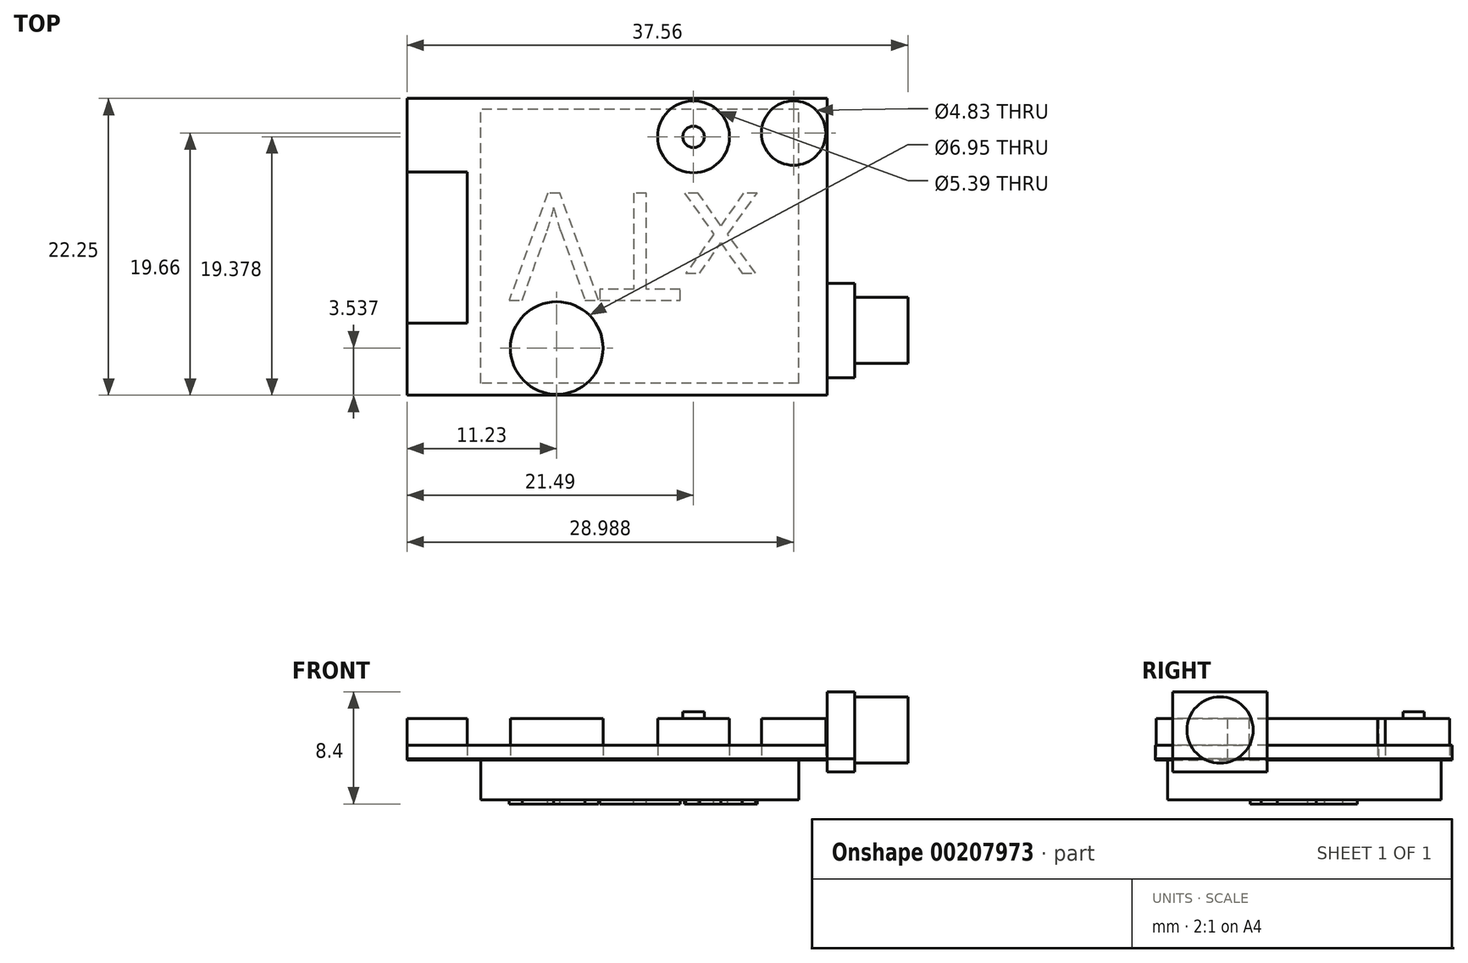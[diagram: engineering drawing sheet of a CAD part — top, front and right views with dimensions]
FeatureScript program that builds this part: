
annotation { "Feature Type Name" : "Feature", "Feature Type Description" : "" }
export const myFeature = defineFeature(function(context is Context, id is Id, definition is map)
    precondition{}
    {
        {
            var Q0;
            Q0=qCreatedBy(makeId("Top.planeOp"),FACE);
            var sketch = newSketch(context, id + "F0", { "sketchPlane" : qUnion([Q0])});
            skLineSegment(sketch, "E0.bottom", {"start": v(38.2, 11.57) * mm, "end": v(6.7, 11.57) * mm});
            skLineSegment(sketch, "E0.top", {"start": v(38.2, 33.82) * mm, "end": v(6.7, 33.82) * mm});
            skLineSegment(sketch, "E0.left", {"start": v(38.2, 11.57) * mm, "end": v(38.2, 33.82) * mm});
            skLineSegment(sketch, "E0.right", {"start": v(6.7, 11.57) * mm, "end": v(6.7, 33.82) * mm});
            skLineSegment(sketch, "E1.bottom", {"start": v(6.7, 28.3) * mm, "end": v(11.22, 28.3) * mm});
            skLineSegment(sketch, "E1.top", {"start": v(6.7, 16.97) * mm, "end": v(11.22, 16.97) * mm});
            skLineSegment(sketch, "E1.left", {"start": v(6.7, 28.3) * mm, "end": v(6.7, 16.97) * mm});
            skLineSegment(sketch, "E1.right", {"start": v(11.22, 28.3) * mm, "end": v(11.22, 16.97) * mm});
            skCircle(sketch, "E2", {"center": v(28.19, 30.95) * mm, "radius": 2.7 * mm});
            skCircle(sketch, "E3", {"center": v(35.69, 31.23) * mm, "radius": 2.41 * mm});
            skCircle(sketch, "E4", {"center": v(17.93, 15.1) * mm, "radius": 3.47 * mm});
            skLineSegment(sketch, "E5", {"start": v(38.2, 19.97) * mm, "end": v(40.26, 19.97) * mm});
            skLineSegment(sketch, "E6", {"start": v(40.26, 19.97) * mm, "end": v(40.26, 12.89) * mm});
            skLineSegment(sketch, "E7", {"start": v(40.26, 12.89) * mm, "end": v(38.2, 12.89) * mm});
            skSolve(sketch);
        }
        {
            var Q0;
            Q0=makeQuery(id+"F0.imprint","IMPRINT",FACE,{"disambiguationData":[TD([[makeQuery(id+"F0.imprint","IMPRINT",EDGE,{"derivedFrom":sQuery(id+"F0.wireOp",EDGE,"E1.bottom")}),-1.0]])]});
            var Q1;
            Q1=makeQuery(id+"F0.imprint","IMPRINT",FACE,{"disambiguationData":[TD([[makeQuery(id+"F0.imprint","IMPRINT",EDGE,{"derivedFrom":sQuery(id+"F0.wireOp",EDGE,"E4")}),1.0]])]});
            var Q2;
            Q2=makeQuery(id+"F0.imprint","IMPRINT",FACE,{"disambiguationData":[TD([[makeQuery(id+"F0.imprint","IMPRINT",EDGE,{"derivedFrom":sQuery(id+"F0.wireOp",EDGE,"E2")}),1.0]])]});
            var Q3;
            Q3=makeQuery(id+"F0.imprint","IMPRINT",FACE,{"disambiguationData":[TD([[makeQuery(id+"F0.imprint","IMPRINT",EDGE,{"derivedFrom":sQuery(id+"F0.wireOp",EDGE,"E3")}),1.0]])]});
            extrude(context, id + "F1", {"entities" : qUnion([Q0, Q1, Q2, Q3]), "depth" : 3 * mm});
        }
        {
            var Q0;
            Q0 = qSketchRegion(id + "F0", true);
            extrude(context, id + "F2", {"entities" : qUnion([Q0]), "depth" : 1 * mm});
        }
        {
            var Q0;
            Q0=makeQuery(id+"F2.opExtrude","CAP_FACE",FACE,{"disambiguationData":[OSD([sQuery(id+"F0.wireOp",EDGE,"E0.bottom"),sQuery(id+"F0.wireOp",EDGE,"E0.top"),sQuery(id+"F0.wireOp",EDGE,"E0.left"),sQuery(id+"F0.wireOp",EDGE,"E0.right"),sQuery(id+"F0.wireOp",EDGE,"E1.left"),sQuery(id+"F0.wireOp",EDGE,"E2"),sQuery(id+"F0.wireOp",EDGE,"E3"),sQuery(id+"F0.wireOp",EDGE,"E4")])],"isStart":true});
            var sketch = newSketch(context, id + "F3", { "sketchPlane" : qUnion([Q0])});
            skLineSegment(sketch, "E8.bottom", {"start": v(38.2, -33.82) * mm, "end": v(6.7, -33.82) * mm});
            skLineSegment(sketch, "E8.top", {"start": v(38.2, -11.57) * mm, "end": v(6.7, -11.57) * mm});
            skLineSegment(sketch, "E8.left", {"start": v(38.2, -33.82) * mm, "end": v(38.2, -11.57) * mm});
            skLineSegment(sketch, "E8.right", {"start": v(6.7, -33.82) * mm, "end": v(6.7, -11.57) * mm});
            skSolve(sketch);
        }
        {
            var Q0;
            Q0=makeQuery(id+"F1.opExtrude","CAP_FACE",FACE,{"disambiguationData":[OSD([sQuery(id+"F0.wireOp",EDGE,"E2")])],"isStart":false});
            var sketch = newSketch(context, id + "F4", { "sketchPlane" : qUnion([Q0])});
            skCircle(sketch, "E9", {"center": v(28.19, 30.95) * mm, "radius": 0.8 * mm});
            skSolve(sketch);
        }
        {
            var Q0;
            Q0=makeQuery(id+"F4.imprint","IMPRINT",FACE,{"disambiguationData":[TD([[makeQuery(id+"F4.imprint","IMPRINT",EDGE,{"derivedFrom":sQuery(id+"F4.wireOp",EDGE,"E9")}),1.0]])]});
            extrude(context, id + "F5", {"entities" : qUnion([Q0]), "operationType" : NewBodyOperationType.ADD, "depth" : .5 * mm});
        }
        {
            var Q0;
            Q0=makeQuery(id+"F3.imprint","IMPRINT",FACE,{"disambiguationData":[TD([[makeQuery(id+"F3.imprint","IMPRINT",EDGE,{"derivedFrom":sQuery(id+"F3.wireOp",EDGE,"E8.bottom")}),-1.0]])]});
            var Q1;
            Q1=makeQuery(id+"F3.imprint","IMPRINT",FACE,{"disambiguationData":[TD([[makeQuery(id+"F3.imprint","IMPRINT",EDGE,{"derivedFrom":makeQuery(id+"F2.opExtrude","CAP_EDGE",EDGE,{"disambiguationData":[OSD([sQuery(id+"F0.wireOp",EDGE,"E3")])],"isStart":true})}),-1.0]])]});
            var Q2;
            Q2=makeQuery(id+"F3.imprint","IMPRINT",FACE,{"disambiguationData":[TD([[makeQuery(id+"F3.imprint","IMPRINT",EDGE,{"derivedFrom":makeQuery(id+"F2.opExtrude","CAP_EDGE",EDGE,{"disambiguationData":[OSD([sQuery(id+"F0.wireOp",EDGE,"E2")])],"isStart":true})}),-1.0]])]});
            var Q3;
            Q3=makeQuery(id+"F3.imprint","IMPRINT",FACE,{"disambiguationData":[TD([[makeQuery(id+"F3.imprint","IMPRINT",EDGE,{"derivedFrom":makeQuery(id+"F2.opExtrude","CAP_EDGE",EDGE,{"disambiguationData":[OSD([sQuery(id+"F0.wireOp",EDGE,"E4")])],"isStart":true})}),-1.0]])]});
            extrude(context, id + "F6", {"entities" : qUnion([Q0, Q1, Q2, Q3]), "depth" : .1 * mm});
        }
        {
            var Q0;
            Q0=makeQuery(id+"F6.opExtrude","CAP_FACE",FACE,{"disambiguationData":[OSD([sQuery(id+"F3.wireOp",EDGE,"E8.bottom"),sQuery(id+"F3.wireOp",EDGE,"E8.top"),sQuery(id+"F3.wireOp",EDGE,"E8.left"),sQuery(id+"F3.wireOp",EDGE,"E8.right")])],"isStart":false});
            var sketch = newSketch(context, id + "F7", { "sketchPlane" : qUnion([Q0])});
            skLineSegment(sketch, "E10.bottom", {"start": v(36.07, -12.48) * mm, "end": v(12.23, -12.48) * mm});
            skLineSegment(sketch, "E10.top", {"start": v(36.07, -33) * mm, "end": v(12.23, -33) * mm});
            skLineSegment(sketch, "E10.left", {"start": v(36.07, -12.48) * mm, "end": v(36.07, -33) * mm});
            skLineSegment(sketch, "E10.right", {"start": v(12.23, -12.48) * mm, "end": v(12.23, -33) * mm});
            skSolve(sketch);
        }
        {
            var Q0;
            Q0=makeQuery(id+"F7.imprint","IMPRINT",FACE,{"disambiguationData":[TD([[makeQuery(id+"F7.imprint","IMPRINT",EDGE,{"derivedFrom":sQuery(id+"F7.wireOp",EDGE,"E10.bottom")}),1.0]])]});
            extrude(context, id + "F8", {"entities" : qUnion([Q0]), "operationType" : NewBodyOperationType.ADD, "depth" : 3 * mm});
        }
        {
            var Q0;
            Q0=makeQuery(id+"F8.opExtrude","CAP_FACE",FACE,{"disambiguationData":[OSD([sQuery(id+"F7.wireOp",EDGE,"E10.bottom"),sQuery(id+"F7.wireOp",EDGE,"E10.top"),sQuery(id+"F7.wireOp",EDGE,"E10.left"),sQuery(id+"F7.wireOp",EDGE,"E10.right")])],"isStart":false});
            var sketch = newSketch(context, id + "F9", { "sketchPlane" : qUnion([Q0])});
            skText(sketch, "E11", { "text": "VTx", "fontName": "OpenSans-Regular.ttf"});
            const initialGuessF9  = {"E11": [0.01437, -0.02673, 1, 0, 0.0081]};
            skSetInitialGuess(sketch, initialGuessF9);
            skSolve(sketch);
        }
        {
            var Q0;
            Q0=makeQuery(id+"F9.imprint","IMPRINT",FACE,{"disambiguationData":[TD([[makeQuery(id+"F9.imprint","IMPRINT",EDGE,{"derivedFrom":sQuery(id+"F9.wireOp",EDGE,"E11.sketch_text.stroke-0")}),-1.0]])]});
            var Q1;
            Q1=makeQuery(id+"F9.imprint","IMPRINT",FACE,{"disambiguationData":[TD([[makeQuery(id+"F9.imprint","IMPRINT",EDGE,{"derivedFrom":sQuery(id+"F9.wireOp",EDGE,"E11.sketch_text.stroke-9")}),-1.0]])]});
            var Q2;
            Q2=makeQuery(id+"F9.imprint","IMPRINT",FACE,{"disambiguationData":[TD([[makeQuery(id+"F9.imprint","IMPRINT",EDGE,{"derivedFrom":sQuery(id+"F9.wireOp",EDGE,"E11.sketch_text.stroke-17")}),-1.0]])]});
            extrude(context, id + "F10", {"entities" : qUnion([Q0, Q1, Q2]), "operationType" : NewBodyOperationType.ADD, "depth" : .3 * mm});
        }
        {
            var Q0;
            Q0=makeQuery(id+"F2.opExtrude","CAP_FACE",FACE,{"disambiguationData":[OSD([sQuery(id+"F0.wireOp",EDGE,"E0.bottom"),sQuery(id+"F0.wireOp",EDGE,"E0.top"),sQuery(id+"F0.wireOp",EDGE,"E0.left"),sQuery(id+"F0.wireOp",EDGE,"E0.right"),sQuery(id+"F0.wireOp",EDGE,"E1.left"),sQuery(id+"F0.wireOp",EDGE,"E2"),sQuery(id+"F0.wireOp",EDGE,"E3"),sQuery(id+"F0.wireOp",EDGE,"E4"),sQuery(id+"F0.wireOp",EDGE,"E5"),sQuery(id+"F0.wireOp",EDGE,"E6"),sQuery(id+"F0.wireOp",EDGE,"E7")])],"isStart":false});
            var sketch = newSketch(context, id + "F11", { "sketchPlane" : qUnion([Q0])});
            skLineSegment(sketch, "E12", {"start": v(38.2, 19.97) * mm, "end": v(38.2, 12.89) * mm});
            skSolve(sketch);
        }
        {
            var Q0;
            Q0=makeQuery(id+"F11.imprint","IMPRINT",FACE,{"disambiguationData":[TD([[makeQuery(id+"F11.imprint","IMPRINT",EDGE,{"derivedFrom":sQuery(id+"F11.wireOp",EDGE,"E12")}),1.0]])]});
            extrude(context, id + "F12", {"entities" : qUnion([Q0]), "operationType" : NewBodyOperationType.ADD, "depth" : 4 * mm});
        }
        {
            var Q0;
            Q0=makeQuery(id+"F2.opExtrude","CAP_FACE",FACE,{"disambiguationData":[OSD([sQuery(id+"F0.wireOp",EDGE,"E0.bottom"),sQuery(id+"F0.wireOp",EDGE,"E0.top"),sQuery(id+"F0.wireOp",EDGE,"E0.left"),sQuery(id+"F0.wireOp",EDGE,"E0.right"),sQuery(id+"F0.wireOp",EDGE,"E1.left"),sQuery(id+"F0.wireOp",EDGE,"E2"),sQuery(id+"F0.wireOp",EDGE,"E3"),sQuery(id+"F0.wireOp",EDGE,"E4"),sQuery(id+"F0.wireOp",EDGE,"E5"),sQuery(id+"F0.wireOp",EDGE,"E6"),sQuery(id+"F0.wireOp",EDGE,"E7")])],"isStart":true});
            var sketch = newSketch(context, id + "F13", { "sketchPlane" : qUnion([Q0])});
            skLineSegment(sketch, "E13", {"start": v(38.2, -12.89) * mm, "end": v(38.2, -19.97) * mm});
            skSolve(sketch);
        }
        {
            var Q0;
            Q0=makeQuery(id+"F13.imprint","IMPRINT",FACE,{"disambiguationData":[TD([[makeQuery(id+"F13.imprint","IMPRINT",EDGE,{"derivedFrom":sQuery(id+"F13.wireOp",EDGE,"E13")}),1.0]])]});
            extrude(context, id + "F14", {"entities" : qUnion([Q0]), "depth" : 1 * mm});
        }
        {
            var Q0;
            {var subQ0=sQuery(id+"F0.wireOp",EDGE,"E6");Q0=makeQuery(id+"F12.boolean.opBoolean","MERGE",FACE,{"derivedFrom":[makeQuery(id+"F2.opExtrude","SWEPT_FACE",FACE,{"disambiguationData":[OSD([subQ0])]}),makeQuery(id+"F12.opExtrude","SWEPT_FACE",FACE,{"disambiguationData":[OSD([subQ0])]})]});}
            var sketch = newSketch(context, id + "F15", { "sketchPlane" : qUnion([Q0])});
            skLineSegment(sketch, "E14", {"start": v(16.43, 5) * mm, "end": v(16.43, 0) * mm, "construction": true});
            skCircle(sketch, "E15", {"center": v(16.43, 2.14) * mm, "radius": 2.48 * mm});
            skSolve(sketch);
        }
        {
            var Q0;
            {var subQ0=sQuery(id+"F15.wireOp",EDGE,"E15");var subQ1=makeQuery(id+"F2.opExtrude","CAP_EDGE",EDGE,{"disambiguationData":[OSD([sQuery(id+"F0.wireOp",EDGE,"E6")])],"isStart":true});var subQ2=makeQuery(id+"F15.imprint","INTERSECT",VERTEX,{"disambiguationData":[OD(0.0)],"derivedFrom":[subQ1,subQ0]});Q0=makeQuery(id+"F15.imprint","IMPRINT",FACE,{"disambiguationData":[TD([[makeQuery(id+"F15.imprint","IMPRINT",EDGE,{"disambiguationData":[TD([[subQ2,-1.0]])],"derivedFrom":subQ0}),1.0]])]});}
            var Q1;
            {var subQ0=sQuery(id+"F15.wireOp",EDGE,"E15");var subQ1=makeQuery(id+"F2.opExtrude","CAP_EDGE",EDGE,{"disambiguationData":[OSD([sQuery(id+"F0.wireOp",EDGE,"E6")])],"isStart":true});var subQ2=makeQuery(id+"F15.imprint","INTERSECT",VERTEX,{"disambiguationData":[OD(0.0)],"derivedFrom":[subQ1,subQ0]});Q1=makeQuery(id+"F15.imprint","IMPRINT",FACE,{"disambiguationData":[TD([[makeQuery(id+"F15.imprint","IMPRINT",EDGE,{"disambiguationData":[TD([[subQ2,1.0]])],"derivedFrom":subQ0}),1.0]])]});}
            extrude(context, id + "F16", {"entities" : qUnion([Q0, Q1]), "depth" : 4 * mm});
        }
    });
